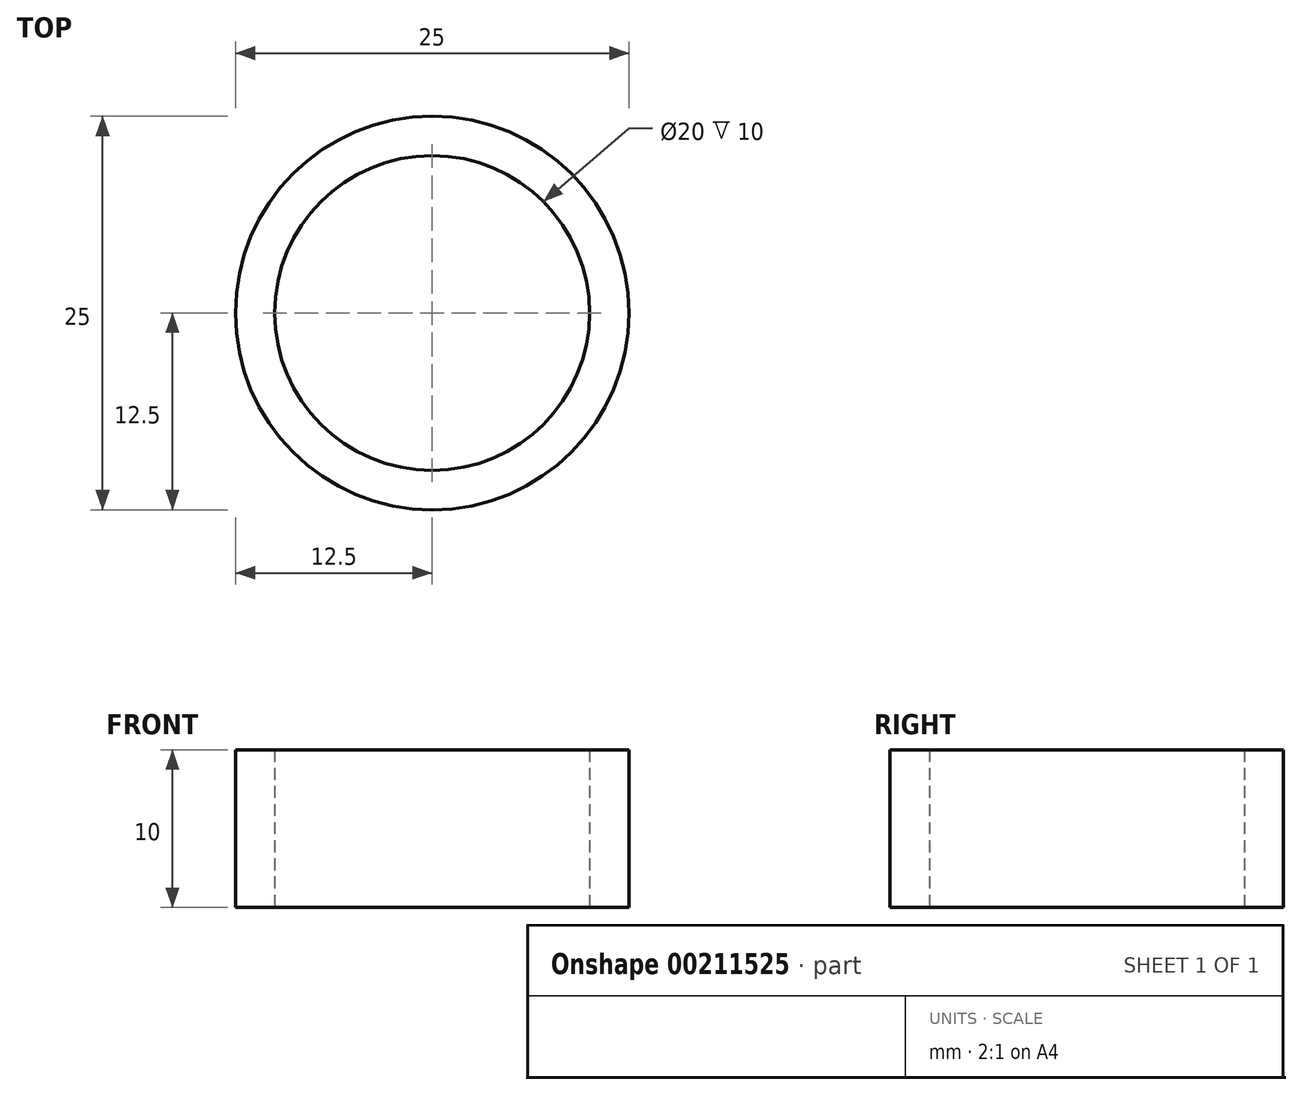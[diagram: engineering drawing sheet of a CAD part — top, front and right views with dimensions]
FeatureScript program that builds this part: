
annotation { "Feature Type Name" : "Feature", "Feature Type Description" : "" }
export const myFeature = defineFeature(function(context is Context, id is Id, definition is map)
    precondition{}
    {
        {
            var Q0;
            Q0=qCreatedBy(makeId("Top.planeOp"),FACE);
            var sketch = newSketch(context, id + "F0", { "sketchPlane" : qUnion([Q0])});
            skCircle(sketch, "E0", {"center": v(0, 0) * mm, "radius": 10 * mm});
            skCircle(sketch, "E1", {"center": v(0, 0) * mm, "radius": 12.5 * mm});
            skSolve(sketch);
        }
        {
            var Q0;
            Q0 = qSketchRegion(id + "F0", true);
            extrude(context, id + "F1", {"entities" : qUnion([Q0]), "flatOperationType" : FlatOperationType.REMOVE, "offsetDistance" : 25.4 * mm, "depth" : 10 * mm, "domain" : OperationDomain.MODEL});
        }
    });
